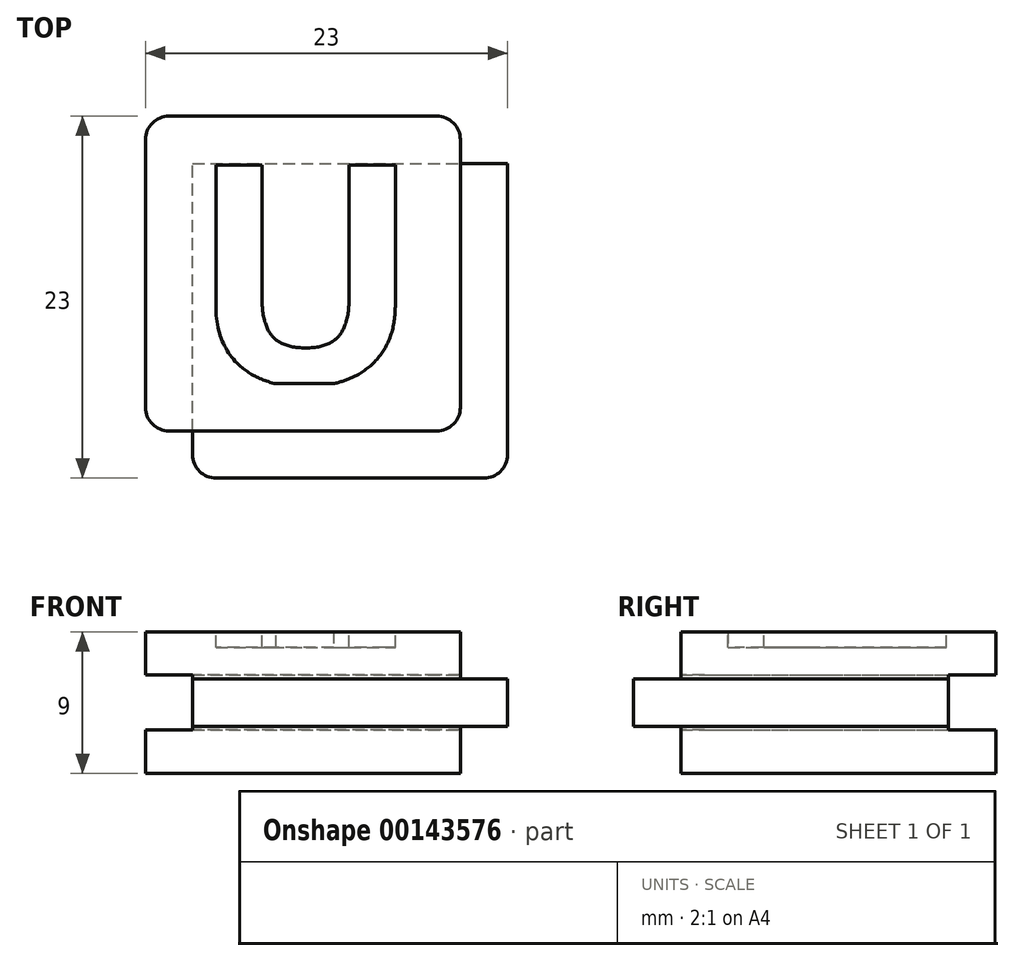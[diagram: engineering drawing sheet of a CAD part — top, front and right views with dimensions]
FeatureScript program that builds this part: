
annotation { "Feature Type Name" : "Feature", "Feature Type Description" : "" }
export const myFeature = defineFeature(function(context is Context, id is Id, definition is map)
    precondition{}
    {
        {
            var Q0;
            Q0=qCreatedBy(makeId("Front.planeOp"),FACE);
            var sketch = newSketch(context, id + "F0", { "sketchPlane" : qUnion([Q0])});
            skLineSegment(sketch, "E0.bottom", {"start": v(10, 4.5) * mm, "end": v(-10, 4.5) * mm});
            skLineSegment(sketch, "E0.top", {"start": v(10, -4.5) * mm, "end": v(-10, -4.5) * mm});
            skLineSegment(sketch, "E0.left", {"start": v(10, 4.5) * mm, "end": v(10, -4.5) * mm});
            skLineSegment(sketch, "E0.right", {"start": v(-10, 4.5) * mm, "end": v(-10, -4.5) * mm});
            skPoint(sketch, "E0.middle", {"position": v(0, 0) * mm});
            skLineSegment(sketch, "E1.bottom", {"start": v(13, 1.5) * mm, "end": v(7, 1.5) * mm});
            skLineSegment(sketch, "E1.top", {"start": v(13, -1.5) * mm, "end": v(7, -1.5) * mm});
            skLineSegment(sketch, "E1.left", {"start": v(13, 1.5) * mm, "end": v(13, -1.5) * mm});
            skLineSegment(sketch, "E1.right", {"start": v(7, 1.5) * mm, "end": v(7, -1.5) * mm});
            skPoint(sketch, "E1.middle", {"position": v(10, 0) * mm});
            skLineSegment(sketch, "E2.bottom", {"start": v(7, 1.5) * mm, "end": v(-7, 1.5) * mm});
            skLineSegment(sketch, "E2.top", {"start": v(7, -1.5) * mm, "end": v(-7, -1.5) * mm});
            skLineSegment(sketch, "E2.right", {"start": v(-7, 1.5) * mm, "end": v(-7, -1.5) * mm});
            skLineSegment(sketch, "E3.bottom", {"start": v(-7, -1.5) * mm, "end": v(-10, -1.5) * mm});
            skLineSegment(sketch, "E3.top", {"start": v(-7, 1.5) * mm, "end": v(-10, 1.5) * mm});
            skLineSegment(sketch, "E3.left", {"start": v(-7, -1.5) * mm, "end": v(-7, 1.5) * mm});
            skLineSegment(sketch, "E3.right", {"start": v(-10, -1.5) * mm, "end": v(-10, 1.5) * mm});
            skSolve(sketch);
        }
        {
            var Q0;
            {var subQ5=sQuery(id+"F0.wireOp",EDGE,"E0.bottom");Q0=makeQuery(id+"F0.imprint","IMPRINT",FACE,{"disambiguationData":[TD([[makeQuery(id+"F0.imprint","IMPRINT",EDGE,{"derivedFrom":subQ5}),1.0]])]});}
            var Q1;
            Q1=makeQuery(id+"F0.imprint","IMPRINT",FACE,{"disambiguationData":[TD([[makeQuery(id+"F0.imprint","IMPRINT",EDGE,{"derivedFrom":sQuery(id+"F0.wireOp",EDGE,"E2.bottom")}),1.0]])]});
            var Q2;
            {var subQ5=sQuery(id+"F0.wireOp",EDGE,"E1.left");Q2=makeQuery(id+"F0.imprint","IMPRINT",FACE,{"disambiguationData":[TD([[makeQuery(id+"F0.imprint","IMPRINT",EDGE,{"derivedFrom":subQ5}),-1.0]])]});}
            var Q3;
            {var subQ5=sQuery(id+"F0.wireOp",EDGE,"E1.right");Q3=makeQuery(id+"F0.imprint","IMPRINT",FACE,{"disambiguationData":[TD([[makeQuery(id+"F0.imprint","IMPRINT",EDGE,{"derivedFrom":subQ5}),1.0]])]});}
            var Q4;
            Q4=makeQuery(id+"F0.imprint","IMPRINT",FACE,{"disambiguationData":[TD([[makeQuery(id+"F0.imprint","IMPRINT",EDGE,{"derivedFrom":sQuery(id+"F0.wireOp",EDGE,"E3.bottom")}),-1.0]])]});
            var Q5;
            {var subQ5=sQuery(id+"F0.wireOp",EDGE,"E0.top");Q5=makeQuery(id+"F0.imprint","IMPRINT",FACE,{"disambiguationData":[TD([[makeQuery(id+"F0.imprint","IMPRINT",EDGE,{"derivedFrom":subQ5}),-1.0]])]});}
            extrude(context, id + "F1", {"entities" : qUnion([Q0, Q1, Q2, Q3, Q4, Q5]), "oppositeDirection" : true, "depth" : 20 * mm});
        }
        {
            var Q0;
            Q0=makeQuery(id+"F0.imprint","IMPRINT",FACE,{"disambiguationData":[TD([[makeQuery(id+"F0.imprint","IMPRINT",EDGE,{"derivedFrom":sQuery(id+"F0.wireOp",EDGE,"E3.bottom")}),-1.0]])]});
            var Q1;
            Q1=makeQuery(id+"F0.imprint","IMPRINT",FACE,{"disambiguationData":[TD([[makeQuery(id+"F0.imprint","IMPRINT",EDGE,{"derivedFrom":sQuery(id+"F0.wireOp",EDGE,"E2.bottom")}),1.0]])]});
            var Q2;
            {var subQ5=sQuery(id+"F0.wireOp",EDGE,"E1.right");Q2=makeQuery(id+"F0.imprint","IMPRINT",FACE,{"disambiguationData":[TD([[makeQuery(id+"F0.imprint","IMPRINT",EDGE,{"derivedFrom":subQ5}),1.0]])]});}
            var Q3;
            {var subQ5=sQuery(id+"F0.wireOp",EDGE,"E1.left");Q3=makeQuery(id+"F0.imprint","IMPRINT",FACE,{"disambiguationData":[TD([[makeQuery(id+"F0.imprint","IMPRINT",EDGE,{"derivedFrom":subQ5}),-1.0]])]});}
            extrude(context, id + "F2", {"entities" : qUnion([Q0, Q1, Q2, Q3]), "operationType" : NewBodyOperationType.ADD, "depth" : 3 * mm});
        }
        {
            var Q0;
            {var subQ0=sQuery(id+"F0.wireOp",EDGE,"E1.left");Q0=makeQuery(id+"F2.boolean.opBoolean","MERGE",FACE,{"derivedFrom":[makeQuery(id+"F1.opExtrude","SWEPT_FACE",FACE,{"disambiguationData":[OSD([subQ0])]}),makeQuery(id+"F2.opExtrude","SWEPT_FACE",FACE,{"disambiguationData":[OSD([subQ0])]})]});}
            var sketch = newSketch(context, id + "F3", { "sketchPlane" : qUnion([Q0])});
            skLineSegment(sketch, "E4.bottom", {"start": v(23, 1.75) * mm, "end": v(17, 1.75) * mm});
            skLineSegment(sketch, "E4.top", {"start": v(23, -1.75) * mm, "end": v(17, -1.75) * mm});
            skLineSegment(sketch, "E4.left", {"start": v(23, 1.75) * mm, "end": v(23, -1.75) * mm});
            skLineSegment(sketch, "E4.right", {"start": v(17, 1.75) * mm, "end": v(17, -1.75) * mm});
            skPoint(sketch, "E4.middle", {"position": v(20, 0) * mm});
            skSolve(sketch);
        }
        {
            var Q0;
            {var subQ1=sQuery(id+"F3.wireOp",EDGE,"E4.bottom");Q0=makeQuery(id+"F3.imprint","IMPRINT",FACE,{"disambiguationData":[TD([[makeQuery(id+"F3.imprint","IMPRINT",EDGE,{"derivedFrom":subQ1}),1.0]])]});}
            var Q1;
            {var subQ1=sQuery(id+"F0.wireOp",EDGE,"E1.left");var subQ8=makeQuery(id+"F1.opExtrude","CAP_EDGE",EDGE,{"disambiguationData":[OSD([subQ1])],"isStart":false});Q1=makeQuery(id+"F3.imprint","IMPRINT",FACE,{"disambiguationData":[TD([[makeQuery(id+"F3.imprint","IMPRINT",EDGE,{"derivedFrom":subQ8}),-1.0]])]});}
            extrude(context, id + "F4", {"entities" : qUnion([Q0, Q1]), "operationType" : NewBodyOperationType.REMOVE, "oppositeDirection" : true, "depth" : 100 * mm});
        }
        {
            var Q0;
            Q0=makeQuery(id+"F4.boolean.opBoolean","COPY",FACE,{"derivedFrom":makeQuery(id+"F4.opExtrude","SWEPT_FACE",FACE,{"disambiguationData":[OSD([sQuery(id+"F3.wireOp",EDGE,"E4.right")])]})});
            var sketch = newSketch(context, id + "F5", { "sketchPlane" : qUnion([Q0])});
            skLineSegment(sketch, "E5.bottom", {"start": v(13, 1.75) * mm, "end": v(7, 1.75) * mm});
            skLineSegment(sketch, "E5.top", {"start": v(13, -1.75) * mm, "end": v(7, -1.75) * mm});
            skLineSegment(sketch, "E5.left", {"start": v(13, 1.75) * mm, "end": v(13, -1.75) * mm});
            skLineSegment(sketch, "E5.right", {"start": v(7, 1.75) * mm, "end": v(7, -1.75) * mm});
            skPoint(sketch, "E5.middle", {"position": v(10, 0) * mm});
            skSolve(sketch);
        }
        {
            var Q0;
            {var subQ3=sQuery(id+"F5.wireOp",EDGE,"E5.left");Q0=makeQuery(id+"F5.imprint","IMPRINT",FACE,{"disambiguationData":[TD([[makeQuery(id+"F5.imprint","IMPRINT",EDGE,{"derivedFrom":subQ3}),-1.0]])]});}
            var Q1;
            {var subQ4=sQuery(id+"F5.wireOp",EDGE,"E5.right");Q1=makeQuery(id+"F5.imprint","IMPRINT",FACE,{"disambiguationData":[TD([[makeQuery(id+"F5.imprint","IMPRINT",EDGE,{"derivedFrom":subQ4}),1.0]])]});}
            extrude(context, id + "F6", {"entities" : qUnion([Q0, Q1]), "operationType" : NewBodyOperationType.REMOVE, "oppositeDirection" : true, "depth" : 100 * mm});
        }
        {
            var Q0;
            Q0=makeQuery(id+"F6.boolean.opBoolean","INTERSECT",EDGE,{"derivedFrom":[makeQuery(id+"F2.opExtrude","CAP_FACE",FACE,{"disambiguationData":[OSD([sQuery(id+"F0.wireOp",EDGE,"E1.bottom"),sQuery(id+"F0.wireOp",EDGE,"E1.top"),sQuery(id+"F0.wireOp",EDGE,"E1.left"),sQuery(id+"F0.wireOp",EDGE,"E2.bottom"),sQuery(id+"F0.wireOp",EDGE,"E2.top"),sQuery(id+"F0.wireOp",EDGE,"E3.bottom"),sQuery(id+"F0.wireOp",EDGE,"E3.top"),sQuery(id+"F0.wireOp",EDGE,"E3.right")])],"isStart":false}),makeQuery(id+"F6.opExtrude","SWEPT_FACE",FACE,{"disambiguationData":[OSD([sQuery(id+"F5.wireOp",EDGE,"E5.right")])]})]});
            var Q1;
            Q1=makeQuery(id+"F2.opExtrude","CAP_EDGE",EDGE,{"disambiguationData":[OSD([sQuery(id+"F0.wireOp",EDGE,"E1.left")])],"isStart":false});
            var Q2;
            {var subQ0=sQuery(id+"F0.wireOp",EDGE,"E0.left");Q2=makeQuery(id+"F1.opExtrude","CAP_EDGE",EDGE,{"disambiguationData":[OSD([subQ0]),TDD([makeQuery(id+"F0.imprint","IMPRINT",EDGE,{"disambiguationData":[TD([[makeQuery(id+"F0.imprint","INTERSECT",VERTEX,{"derivedFrom":[sQuery(id+"F0.wireOp",EDGE,"E0.bottom"),subQ0]}),-1.0]])],"derivedFrom":subQ0})])],"isStart":true});}
            var Q3;
            {var subQ0=sQuery(id+"F0.wireOp",EDGE,"E0.left");Q3=makeQuery(id+"F1.opExtrude","CAP_EDGE",EDGE,{"disambiguationData":[OSD([subQ0]),TDD([makeQuery(id+"F0.imprint","IMPRINT",EDGE,{"disambiguationData":[TD([[makeQuery(id+"F0.imprint","INTERSECT",VERTEX,{"derivedFrom":[sQuery(id+"F0.wireOp",EDGE,"E0.top"),subQ0]}),1.0]])],"derivedFrom":subQ0})])],"isStart":true});}
            var Q4;
            {var subQ0=sQuery(id+"F0.wireOp",EDGE,"E3.right");var subQ1=sQuery(id+"F0.wireOp",EDGE,"E0.right");var subQ3=sQuery(id+"F0.wireOp",EDGE,"E0.top");Q4=makeQuery(id+"F2.boolean.opBoolean","SPLIT",EDGE,{"disambiguationData":[TD([makeQuery(id+"F1.opExtrude","SWEPT_FACE",FACE,{"disambiguationData":[OSD([subQ3])]})])],"derivedFrom":makeQuery(id+"F1.opExtrude","CAP_EDGE",EDGE,{"disambiguationData":[OSD([subQ1,subQ0])],"isStart":true})});}
            var Q5;
            {var subQ1=sQuery(id+"F0.wireOp",EDGE,"E3.right");var subQ2=sQuery(id+"F0.wireOp",EDGE,"E0.right");var subQ3=sQuery(id+"F0.wireOp",EDGE,"E0.bottom");Q5=makeQuery(id+"F2.boolean.opBoolean","SPLIT",EDGE,{"disambiguationData":[TD([makeQuery(id+"F1.opExtrude","SWEPT_FACE",FACE,{"disambiguationData":[OSD([subQ3])]})])],"derivedFrom":makeQuery(id+"F1.opExtrude","CAP_EDGE",EDGE,{"disambiguationData":[OSD([subQ2,subQ1])],"isStart":true})});}
            var Q6;
            Q6=makeQuery(id+"F6.boolean.opBoolean","COPY",EDGE,{"derivedFrom":makeQuery(id+"F6.opExtrude","CAP_EDGE",EDGE,{"disambiguationData":[OSD([sQuery(id+"F5.wireOp",EDGE,"E5.right")])],"isStart":true})});
            var Q7;
            {var subQ0=sQuery(id+"F0.wireOp",EDGE,"E3.right");var subQ1=sQuery(id+"F0.wireOp",EDGE,"E0.right");var subQ2=sQuery(id+"F0.wireOp",EDGE,"E0.bottom");Q7=makeQuery(id+"F4.boolean.opBoolean","SPLIT",EDGE,{"disambiguationData":[TD([makeQuery(id+"F1.opExtrude","SWEPT_FACE",FACE,{"disambiguationData":[OSD([subQ2])]})])],"derivedFrom":makeQuery(id+"F1.opExtrude","CAP_EDGE",EDGE,{"disambiguationData":[OSD([subQ1,subQ0])],"isStart":false})});}
            var Q8;
            {var subQ0=sQuery(id+"F0.wireOp",EDGE,"E3.right");var subQ1=sQuery(id+"F0.wireOp",EDGE,"E0.right");var subQ2=sQuery(id+"F0.wireOp",EDGE,"E0.top");Q8=makeQuery(id+"F4.boolean.opBoolean","SPLIT",EDGE,{"disambiguationData":[TD([makeQuery(id+"F1.opExtrude","SWEPT_FACE",FACE,{"disambiguationData":[OSD([subQ2])]})])],"derivedFrom":makeQuery(id+"F1.opExtrude","CAP_EDGE",EDGE,{"disambiguationData":[OSD([subQ1,subQ0])],"isStart":false})});}
            var Q9;
            Q9=makeQuery(id+"F4.boolean.opBoolean","COPY",EDGE,{"derivedFrom":makeQuery(id+"F4.opExtrude","CAP_EDGE",EDGE,{"disambiguationData":[OSD([sQuery(id+"F3.wireOp",EDGE,"E4.right")])],"isStart":true})});
            var Q10;
            {var subQ0=sQuery(id+"F0.wireOp",EDGE,"E0.left");Q10=makeQuery(id+"F1.opExtrude","CAP_EDGE",EDGE,{"disambiguationData":[OSD([subQ0]),TDD([makeQuery(id+"F0.imprint","IMPRINT",EDGE,{"disambiguationData":[TD([[makeQuery(id+"F0.imprint","INTERSECT",VERTEX,{"derivedFrom":[sQuery(id+"F0.wireOp",EDGE,"E0.bottom"),subQ0]}),-1.0]])],"derivedFrom":subQ0})])],"isStart":false});}
            var Q11;
            {var subQ0=sQuery(id+"F0.wireOp",EDGE,"E0.left");Q11=makeQuery(id+"F1.opExtrude","CAP_EDGE",EDGE,{"disambiguationData":[OSD([subQ0]),TDD([makeQuery(id+"F0.imprint","IMPRINT",EDGE,{"disambiguationData":[TD([[makeQuery(id+"F0.imprint","INTERSECT",VERTEX,{"derivedFrom":[sQuery(id+"F0.wireOp",EDGE,"E0.top"),subQ0]}),1.0]])],"derivedFrom":subQ0})])],"isStart":false});}
            fillet(context, id + "F7", {"entities" : qUnion([Q0, Q1, Q2, Q3, Q4, Q5, Q6, Q7, Q8, Q9, Q10, Q11]), "radius" : 1.5 * mm, "tangentPropagation" : true, "allowEdgeOverflow" : false});
        }
        {
            var Q0;
            Q0=makeQuery(id+"F1.opExtrude","SWEPT_FACE",FACE,{"disambiguationData":[OSD([sQuery(id+"F0.wireOp",EDGE,"E0.bottom")])]});
            var sketch = newSketch(context, id + "F8", { "sketchPlane" : qUnion([Q0])});
            skText(sketch, "E6", { "text": "U", "fontName": "OpenSans-Bold.ttf"});
            skLineSegment(sketch, "E7.0", {"start": v(11.01, 3) * mm, "end": v(-11.07, 3) * mm});
            const initialGuessF8  = {"E6": [-0.00718, 0.003, 1, 0, 0.014]};
            skSetInitialGuess(sketch, initialGuessF8);
            skSolve(sketch);
        }
        {
            var Q0;
            Q0=makeQuery(id+"F8.imprint","IMPRINT",FACE,{"disambiguationData":[TD([[makeQuery(id+"F8.imprint","IMPRINT",EDGE,{"derivedFrom":sQuery(id+"F8.wireOp",EDGE,"E6.sketch_text.stroke-0")}),-1.0]])]});
            extrude(context, id + "F9", {"entities" : qUnion([Q0]), "operationType" : NewBodyOperationType.REMOVE, "oppositeDirection" : true, "depth" : 1 * mm});
        }
    });
